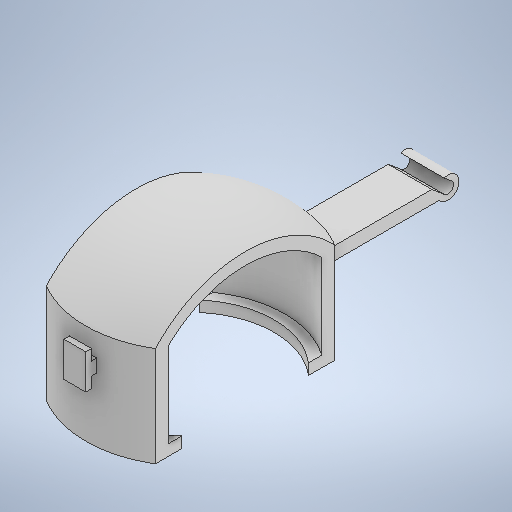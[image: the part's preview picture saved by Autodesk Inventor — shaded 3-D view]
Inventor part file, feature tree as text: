
AUTODESK INVENTOR PART (.ipt)
format: ipt  version: 2025 (Build 290162010, 162A)  size: 317,440 bytes
history: native  units: in
note: dims shown in document units (in); Inventor stores cm internally (conversion verified against a paired STEP export)
features: sketch x4, extrude x3, revolve x1
ambient origin geometry x8: Origin, YZ Plane, XZ Plane, XY Plane, X Axis, Y Axis, Z Axis, Center Point
bodies: Body1 (feature_tree)
feature tree (8):
  revolve  "Revolution1"  [1 undecoded]
  extrude  "Extrusion2"  Depth=0.25in
  extrude  "Extrusion3"  TaperAngle=360.0deg  [1 undecoded]
  extrude  "Extrusion4"  Depth=1.0in TaperAngle=0.0deg
  sketch  "Sketch3"  dims[d7=4.31in d9=2.95in]
  sketch  "Sketch4"  dims[d10=1.95in d11=0.25in]
  sketch  "Sketch5"  dims[d13=0.24in d14=360.0deg]
  sketch  "Sketch6"  dims[d15=2.5in d16=1.0in d17=0.0in d18=0.3in d19=3.0in d20=0.25in d21=0.5in d22=0.3436in d23=1.0in d24=0.0in d25=0.8in d26=0.25in d27=0.25in d28=0.12in d29=0.25in d30=0.12in d31=0.5in d32=0.0in]
note: 2 required parameter values undecoded (feature->parameter linkage not recoverable at this tier; creation-order binding heuristic only, values carry confidence <= 0.55)